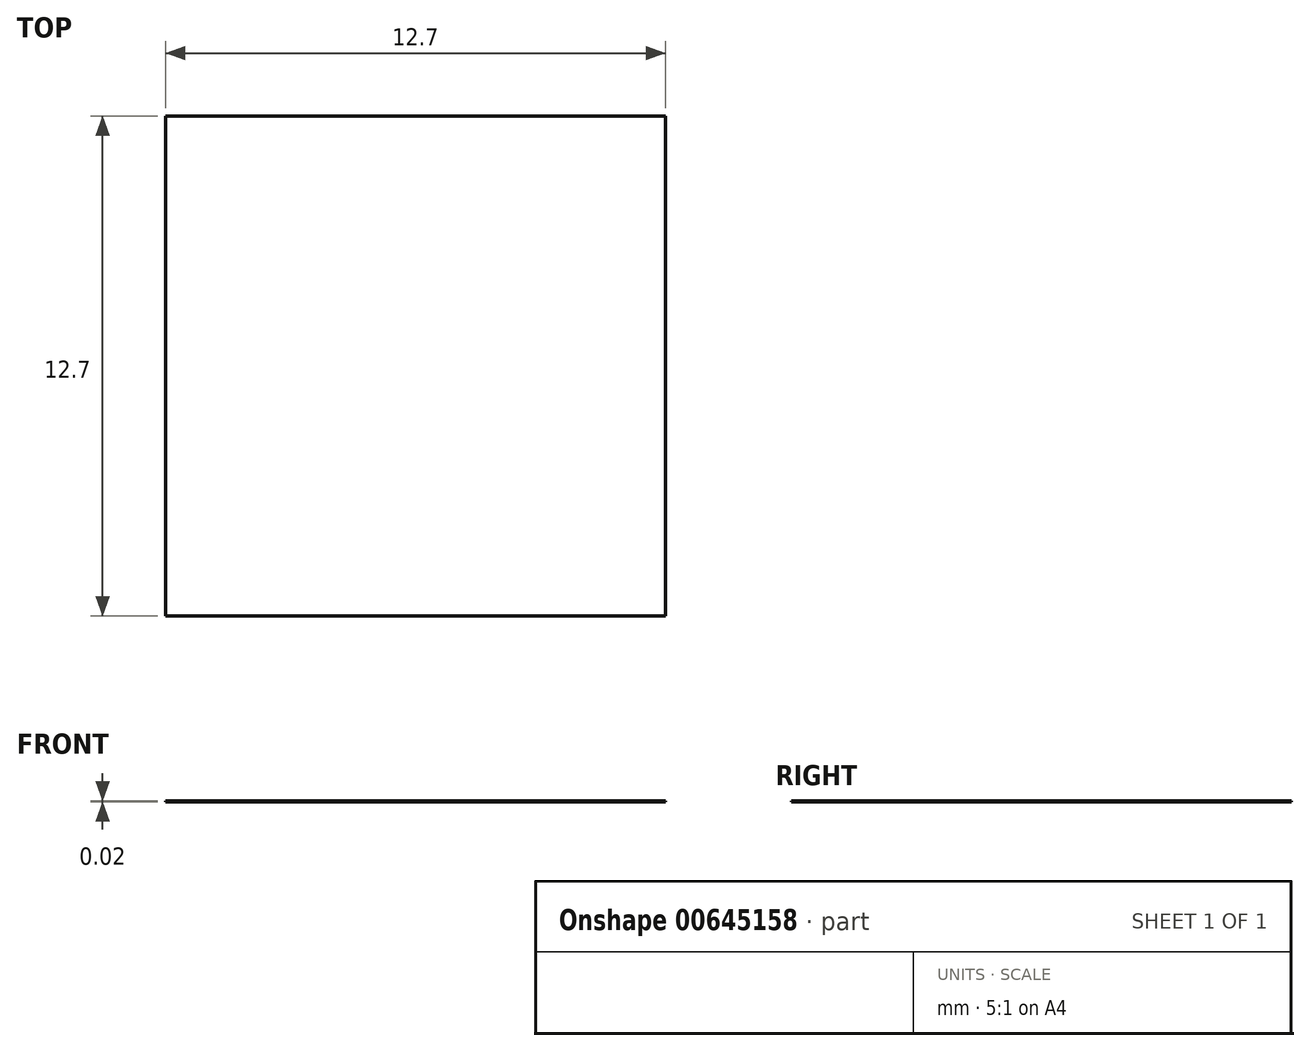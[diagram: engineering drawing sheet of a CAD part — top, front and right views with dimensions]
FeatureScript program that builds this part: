
annotation { "Feature Type Name" : "Feature", "Feature Type Description" : "" }
export const myFeature = defineFeature(function(context is Context, id is Id, definition is map)
    precondition{}
    {
        {
            var Q0;
            Q0=qCreatedBy(makeId("Top.planeOp"),FACE);
            var sketch = newSketch(context, id + "F0", { "sketchPlane" : qUnion([Q0])});
            skLineSegment(sketch, "E0.bottom", {"start": v(6.35, 6.35) * mm, "end": v(-6.35, 6.35) * mm});
            skLineSegment(sketch, "E0.top", {"start": v(6.35, -6.35) * mm, "end": v(-6.35, -6.35) * mm});
            skLineSegment(sketch, "E0.left", {"start": v(6.35, 6.35) * mm, "end": v(6.35, -6.35) * mm});
            skLineSegment(sketch, "E0.right", {"start": v(-6.35, 6.35) * mm, "end": v(-6.35, -6.35) * mm});
            skPoint(sketch, "E0.middle", {"position": v(0, 0) * mm});
            skSolve(sketch);
        }
        {
            var Q0;
            Q0=makeQuery(id+"F0.imprint","IMPRINT",FACE,{"disambiguationData":[TD([[makeQuery(id+"F0.imprint","IMPRINT",EDGE,{"derivedFrom":sQuery(id+"F0.wireOp",EDGE,"E0.bottom")}),1.0]])]});
            extrude(context, id + "F1", {"entities" : qUnion([Q0]), "depth" : 1 / 50.8 * mm, "offsetDistance" : 25.4 * mm});
        }
    });
